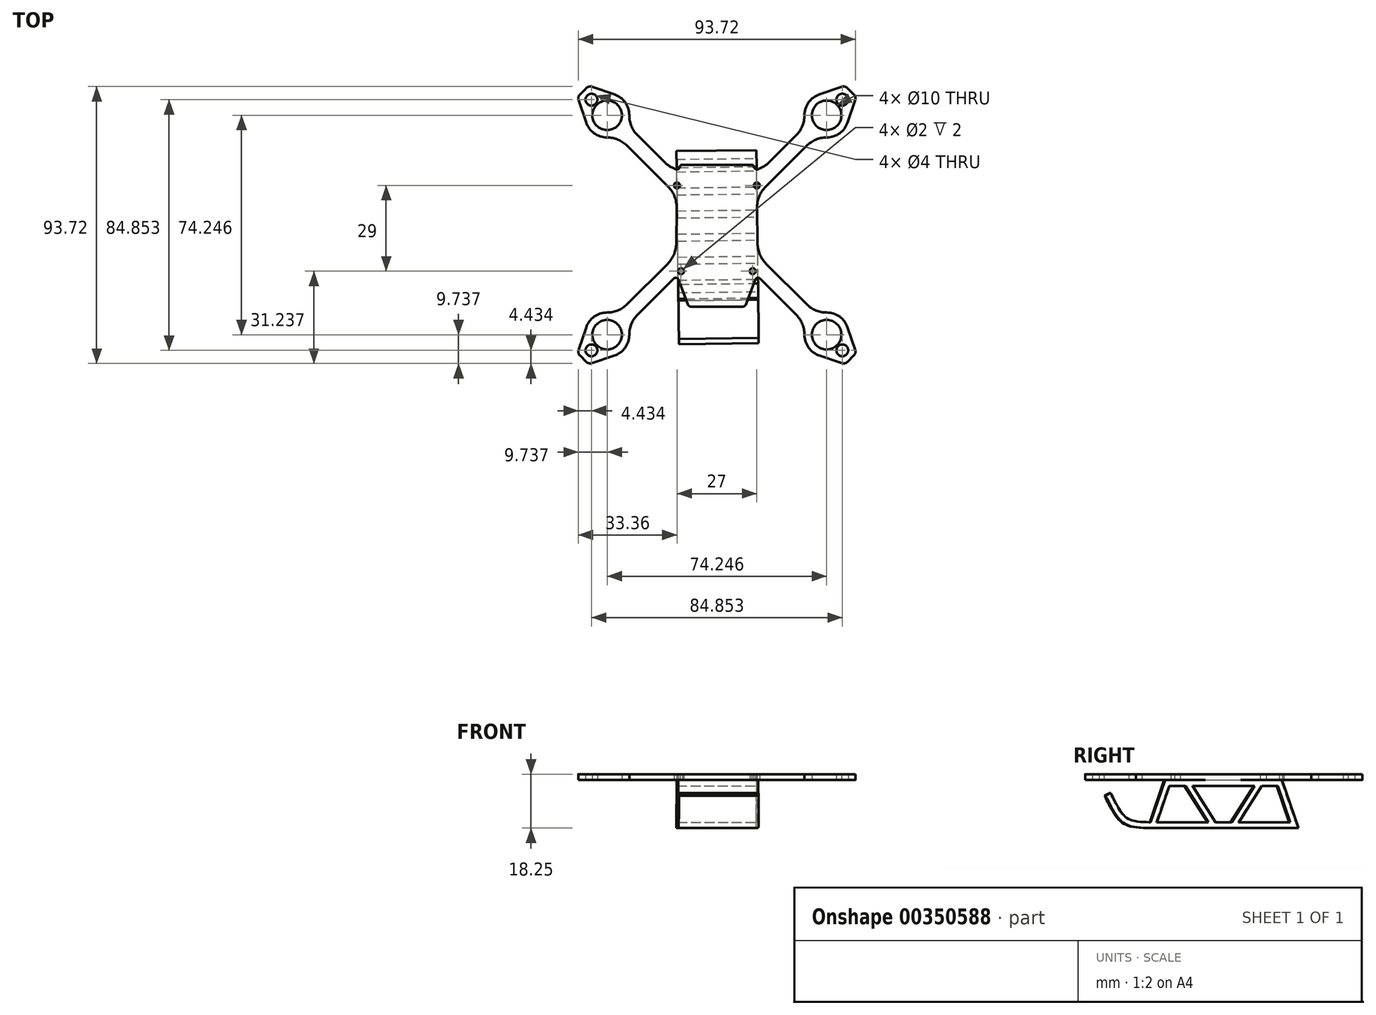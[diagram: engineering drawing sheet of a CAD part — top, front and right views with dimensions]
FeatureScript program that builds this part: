
annotation { "Feature Type Name" : "Feature", "Feature Type Description" : "" }
export const myFeature = defineFeature(function(context is Context, id is Id, definition is map)
    precondition{}
    {
        {
            var Q0;
            Q0=qCreatedBy(makeId("Top.planeOp"),FACE);
            var sketch = newSketch(context, id + "F0", { "sketchPlane" : qUnion([Q0])});
            skCircle(sketch, "E0", {"center": v(0, 0) * mm, "radius": 52.5 * mm, "construction": true});
            skLineSegment(sketch, "E1", {"start": v(0, 65.88) * mm, "end": v(0, -68.03) * mm, "construction": true});
            skLineSegment(sketch, "E2", {"start": v(68.65, 0) * mm, "end": v(-69.75, 0) * mm, "construction": true});
            skLineSegment(sketch, "E3.bottom", {"start": v(-52.5, 52.5) * mm, "end": v(52.5, 52.5) * mm, "construction": true});
            skLineSegment(sketch, "E3.top", {"start": v(-52.5, -52.5) * mm, "end": v(52.5, -52.5) * mm, "construction": true});
            skLineSegment(sketch, "E3.left", {"start": v(-52.5, 52.5) * mm, "end": v(-52.5, -52.5) * mm, "construction": true});
            skLineSegment(sketch, "E3.right", {"start": v(52.5, 52.5) * mm, "end": v(52.5, -52.5) * mm, "construction": true});
            skLineSegment(sketch, "E4", {"start": v(-52.5, 52.5) * mm, "end": v(52.5, -52.5) * mm, "construction": true});
            skLineSegment(sketch, "E5", {"start": v(52.5, 52.5) * mm, "end": v(-52.5, -52.5) * mm, "construction": true});
            skCircle(sketch, "E6.MirrorC", {"center": v(-37.12, 37.12) * mm, "radius": 5 * mm});
            skCircle(sketch, "E7.MirrorC", {"center": v(-37.12, -37.12) * mm, "radius": 5 * mm});
            skLineSegment(sketch, "E8", {"start": v(37.12, -37.12) * mm, "end": v(37.12, -15.62) * mm, "construction": true});
            skLineSegment(sketch, "E9", {"start": v(37.12, -15.62) * mm, "end": v(12.12, -15.62) * mm, "construction": true});
            skLineSegment(sketch, "E10", {"start": v(12.12, -15.62) * mm, "end": v(-12.12, -15.62) * mm, "construction": true});
            skLineSegment(sketch, "E11", {"start": v(-12.12, -15.62) * mm, "end": v(-37.12, -15.62) * mm, "construction": true});
            skLineSegment(sketch, "E12", {"start": v(-37.12, -37.12) * mm, "end": v(-37.12, 37.12) * mm, "construction": true});
            skLineSegment(sketch, "E13", {"start": v(37.12, 37.12) * mm, "end": v(37.12, -37.12) * mm, "construction": true});
            skLineSegment(sketch, "E14", {"start": v(37.12, -37.12) * mm, "end": v(-37.12, -37.12) * mm, "construction": true});
            skLineSegment(sketch, "E15", {"start": v(-37.12, 37.12) * mm, "end": v(37.12, 37.12) * mm, "construction": true});
            skCircle(sketch, "E16", {"center": v(-12.12, -15.62) * mm, "radius": 1 * mm});
            skCircle(sketch, "E17.MirrorC", {"center": v(12.12, -15.62) * mm, "radius": 1 * mm});
            skLineSegment(sketch, "E18", {"start": v(37.12, -15.62) * mm, "end": v(37.12, 13.38) * mm, "construction": true});
            skLineSegment(sketch, "E19", {"start": v(37.12, 13.38) * mm, "end": v(13.5, 13.38) * mm, "construction": true});
            skLineSegment(sketch, "E20", {"start": v(13.5, 13.38) * mm, "end": v(4.8, 13.38) * mm, "construction": true});
            skLineSegment(sketch, "E21", {"start": v(-13.5, 13.38) * mm, "end": v(-37.12, 13.38) * mm, "construction": true});
            skCircle(sketch, "E22", {"center": v(-13.5, 13.38) * mm, "radius": 1 * mm});
            skCircle(sketch, "E23.MirrorC", {"center": v(13.5, 13.38) * mm, "radius": 1 * mm});
            skArc(sketch, "E24", {"start": v(-37.12, -29.62) * mm, "mid": v(-41.5, -31.03) * mm, "end": v(-44.22, -34.71) * mm});
            skCircle(sketch, "E25", {"center": v(-42.43, -42.43) * mm, "radius": 2 * mm});
            skLineSegment(sketch, "E26.trimOffspring", {"start": v(-14.61, -18.15) * mm, "end": v(-26.83, -30.37) * mm});
            skLineSegment(sketch, "E27.trimOffspring", {"start": v(26.83, 30.37) * mm, "end": v(17.77, 21.3) * mm});
            skArc(sketch, "E28", {"start": v(-26.83, -30.37) * mm, "mid": v(-28.9, -33.47) * mm, "end": v(-29.62, -37.12) * mm});
            skLineSegment(sketch, "E29", {"start": v(-37.12, -37.12) * mm, "end": v(-17.54, -56.7) * mm, "construction": true});
            skLineSegment(sketch, "E30", {"start": v(-42.17, -46.76) * mm, "end": v(-34.71, -44.22) * mm});
            skLineSegment(sketch, "E31.MirrorCS", {"start": v(-46.76, -42.17) * mm, "end": v(-44.22, -34.71) * mm});
            skLineSegment(sketch, "E32", {"start": v(-46.28, -44.23) * mm, "end": v(-44.23, -46.28) * mm});
            skPoint(sketch, "E33.visualSharp", {"position": v(-43.35, -47.16) * mm});
            skArc(sketch, "E33.filletArc", {"start": v(-44.23, -46.28) * mm, "mid": v(-43.27, -46.81) * mm, "end": v(-42.17, -46.76) * mm});
            skPoint(sketch, "E34.visualSharp", {"position": v(-47.16, -43.35) * mm});
            skArc(sketch, "E34.filletArc", {"start": v(-46.76, -42.17) * mm, "mid": v(-46.81, -43.27) * mm, "end": v(-46.28, -44.23) * mm});
            skLineSegment(sketch, "E35", {"start": v(-43.84, -43.84) * mm, "end": v(-40.1, -47.58) * mm});
            skArc(sketch, "E36.MirrorCS", {"start": v(-30.37, -26.83) * mm, "mid": v(-33.47, -28.9) * mm, "end": v(-37.12, -29.62) * mm});
            skArc(sketch, "E37.trimOffspring", {"start": v(-34.71, -44.22) * mm, "mid": v(-31.03, -41.5) * mm, "end": v(-29.62, -37.12) * mm});
            skLineSegment(sketch, "E38.MirrorCS", {"start": v(26.83, -30.37) * mm, "end": v(11.4, -14.93) * mm});
            skLineSegment(sketch, "E39.MirrorCS", {"start": v(30.37, -26.83) * mm, "end": v(16.67, -13.14) * mm});
            skArc(sketch, "E40.MirrorCS", {"start": v(-30.37, 26.83) * mm, "mid": v(-33.47, 28.9) * mm, "end": v(-37.12, 29.62) * mm});
            skArc(sketch, "E41.MirrorCS", {"start": v(-26.83, 30.37) * mm, "mid": v(-28.9, 33.47) * mm, "end": v(-29.62, 37.12) * mm});
            skArc(sketch, "E42.MirrorCS", {"start": v(-34.71, 44.22) * mm, "mid": v(-31.03, 41.5) * mm, "end": v(-29.62, 37.12) * mm});
            skLineSegment(sketch, "E43.MirrorCS", {"start": v(-42.17, 46.76) * mm, "end": v(-34.71, 44.22) * mm});
            skLineSegment(sketch, "E44.MirrorCS", {"start": v(-46.28, 44.23) * mm, "end": v(-44.23, 46.28) * mm});
            skLineSegment(sketch, "E45.MirrorCS", {"start": v(-46.76, 42.17) * mm, "end": v(-44.22, 34.71) * mm});
            skArc(sketch, "E46.MirrorCS", {"start": v(-37.12, 29.62) * mm, "mid": v(-41.5, 31.03) * mm, "end": v(-44.22, 34.71) * mm});
            skArc(sketch, "E47.MirrorCS", {"start": v(-44.23, 46.28) * mm, "mid": v(-43.27, 46.81) * mm, "end": v(-42.17, 46.76) * mm});
            skArc(sketch, "E48.MirrorCS", {"start": v(-46.76, 42.17) * mm, "mid": v(-46.81, 43.27) * mm, "end": v(-46.28, 44.23) * mm});
            skCircle(sketch, "E49.MirrorC", {"center": v(-42.43, 42.43) * mm, "radius": 2 * mm});
            skLineSegment(sketch, "E50.MirrorCS", {"start": v(0, -65.88) * mm, "end": v(0, 68.03) * mm, "construction": true});
            skArc(sketch, "E51.MirrorCS", {"start": v(44.23, 46.28) * mm, "mid": v(43.27, 46.81) * mm, "end": v(42.17, 46.76) * mm});
            skLineSegment(sketch, "E52.MirrorCS", {"start": v(46.28, 44.23) * mm, "end": v(44.23, 46.28) * mm});
            skArc(sketch, "E53.MirrorCS", {"start": v(46.76, 42.17) * mm, "mid": v(46.81, 43.27) * mm, "end": v(46.28, 44.23) * mm});
            skLineSegment(sketch, "E54.MirrorCS", {"start": v(42.17, 46.76) * mm, "end": v(34.71, 44.22) * mm});
            skArc(sketch, "E55.MirrorCS", {"start": v(30.37, 26.83) * mm, "mid": v(33.47, 28.9) * mm, "end": v(37.12, 29.62) * mm});
            skLineSegment(sketch, "E56.MirrorCS", {"start": v(46.76, 42.17) * mm, "end": v(44.22, 34.71) * mm});
            skCircle(sketch, "E57.MirrorC", {"center": v(37.12, 37.12) * mm, "radius": 5 * mm});
            skArc(sketch, "E58.MirrorCS", {"start": v(34.71, 44.22) * mm, "mid": v(31.03, 41.5) * mm, "end": v(29.62, 37.12) * mm});
            skArc(sketch, "E59.MirrorCS", {"start": v(37.12, 29.62) * mm, "mid": v(41.5, 31.03) * mm, "end": v(44.22, 34.71) * mm});
            skArc(sketch, "E60.MirrorCS", {"start": v(26.83, 30.37) * mm, "mid": v(28.9, 33.47) * mm, "end": v(29.62, 37.12) * mm});
            skCircle(sketch, "E61.MirrorC", {"center": v(42.43, 42.43) * mm, "radius": 2 * mm});
            skArc(sketch, "E62.MirrorCS", {"start": v(46.76, -42.17) * mm, "mid": v(46.81, -43.27) * mm, "end": v(46.28, -44.23) * mm});
            skLineSegment(sketch, "E63.MirrorCS", {"start": v(46.28, -44.23) * mm, "end": v(44.23, -46.28) * mm});
            skArc(sketch, "E64.MirrorCS", {"start": v(44.23, -46.28) * mm, "mid": v(43.27, -46.81) * mm, "end": v(42.17, -46.76) * mm});
            skLineSegment(sketch, "E65.MirrorCS", {"start": v(43.84, -43.84) * mm, "end": v(40.1, -47.58) * mm});
            skLineSegment(sketch, "E66.MirrorCS", {"start": v(46.76, -42.17) * mm, "end": v(44.22, -34.71) * mm});
            skArc(sketch, "E67.MirrorCS", {"start": v(37.12, -29.62) * mm, "mid": v(41.5, -31.03) * mm, "end": v(44.22, -34.71) * mm});
            skCircle(sketch, "E68.MirrorC", {"center": v(42.43, -42.43) * mm, "radius": 2 * mm});
            skArc(sketch, "E69.MirrorCS", {"start": v(30.37, -26.83) * mm, "mid": v(33.47, -28.9) * mm, "end": v(37.12, -29.62) * mm});
            skArc(sketch, "E70.MirrorCS", {"start": v(34.71, -44.22) * mm, "mid": v(31.03, -41.5) * mm, "end": v(29.62, -37.12) * mm});
            skLineSegment(sketch, "E71.MirrorCS", {"start": v(42.17, -46.76) * mm, "end": v(34.71, -44.22) * mm});
            skCircle(sketch, "E72.MirrorC", {"center": v(37.12, -37.12) * mm, "radius": 5 * mm});
            skPoint(sketch, "E73.MirrorP", {"position": v(47.16, -43.35) * mm});
            skPoint(sketch, "E74.MirrorP", {"position": v(43.35, -47.16) * mm});
            skArc(sketch, "E75.MirrorCS", {"start": v(26.83, -30.37) * mm, "mid": v(28.9, -33.47) * mm, "end": v(29.62, -37.12) * mm});
            skPoint(sketch, "E76.orphan", {"position": v(35.83, -32.3) * mm});
            skPoint(sketch, "E77.orphan", {"position": v(32.3, -35.83) * mm});
            skPoint(sketch, "E78.orphan", {"position": v(35.83, 32.3) * mm});
            skPoint(sketch, "E79.orphan", {"position": v(32.3, 35.83) * mm});
            skLineSegment(sketch, "E80", {"start": v(-12.12, -15.62) * mm, "end": v(-12.12, -19.62) * mm, "construction": true});
            skLineSegment(sketch, "E81", {"start": v(-12.12, -19.62) * mm, "end": v(-12.12, -27.62) * mm, "construction": true});
            skLineSegment(sketch, "E82", {"start": v(-8.81, -27.62) * mm, "end": v(0, -27.62) * mm});
            skLineSegment(sketch, "E83", {"start": v(0, -27.62) * mm, "end": v(9.5, -27.62) * mm});
            skCircle(sketch, "E84", {"center": v(-12.12, -15.62) * mm, "radius": 2 * mm, "construction": true});
            skLineSegment(sketch, "E85", {"start": v(-12.97, -18.5) * mm, "end": v(-9.75, -26.98) * mm});
            skArc(sketch, "E86.filletArc", {"start": v(-12.97, -18.5) * mm, "mid": v(-13.7, -17.88) * mm, "end": v(-14.61, -18.15) * mm});
            skPoint(sketch, "E87.visualSharp", {"position": v(-9.5, -27.62) * mm});
            skArc(sketch, "E87.filletArc", {"start": v(-9.75, -26.98) * mm, "mid": v(-9.38, -27.45) * mm, "end": v(-8.81, -27.62) * mm});
            skArc(sketch, "E88.MirrorCS", {"start": v(9.75, -26.98) * mm, "mid": v(9.38, -27.45) * mm, "end": v(8.81, -27.62) * mm});
            skArc(sketch, "E89.MirrorCS", {"start": v(12.97, -18.5) * mm, "mid": v(13.7, -17.88) * mm, "end": v(14.61, -18.15) * mm});
            skLineSegment(sketch, "E90.MirrorCS", {"start": v(12.97, -18.5) * mm, "end": v(9.75, -26.98) * mm});
            skLineSegment(sketch, "E91.trimOffspring", {"start": v(-16.52, 12.99) * mm, "end": v(-30.37, 26.83) * mm});
            skLineSegment(sketch, "E92.trimOffspring", {"start": v(-16.67, -13.14) * mm, "end": v(-30.37, -26.83) * mm});
            skLineSegment(sketch, "E93.MirrorCS", {"start": v(16.52, 12.99) * mm, "end": v(30.37, 26.83) * mm});
            skLineSegment(sketch, "E94.trimOffspring", {"start": v(-17.77, 21.3) * mm, "end": v(-26.83, 30.37) * mm});
            skLineSegment(sketch, "E95", {"start": v(13.75, -6.2) * mm, "end": v(13.6, 5.8) * mm});
            skArc(sketch, "E96.filletArc", {"start": v(13.75, -6.2) * mm, "mid": v(14.53, -9.95) * mm, "end": v(16.67, -13.14) * mm});
            skPoint(sketch, "E97.newPointB", {"position": v(3.54, 0) * mm});
            skArc(sketch, "E97.filletArc", {"start": v(16.52, 12.99) * mm, "mid": v(14.33, 9.69) * mm, "end": v(13.6, 5.8) * mm});
            skArc(sketch, "E98.MirrorCS", {"start": v(-13.75, -6.2) * mm, "mid": v(-14.53, -9.95) * mm, "end": v(-16.67, -13.14) * mm});
            skLineSegment(sketch, "E99.MirrorCS", {"start": v(-13.75, -6.2) * mm, "end": v(-13.6, 5.8) * mm});
            skArc(sketch, "E100.MirrorCS", {"start": v(-16.52, 12.99) * mm, "mid": v(-14.33, 9.69) * mm, "end": v(-13.6, 5.8) * mm});
            skPoint(sketch, "E101.orphan", {"position": v(-3.54, 0) * mm});
            skLineSegment(sketch, "E102", {"start": v(-5.03, 13.38) * mm, "end": v(-5.03, 20.38) * mm, "construction": true});
            skLineSegment(sketch, "E103", {"start": v(4.8, 13.38) * mm, "end": v(4.8, 18.38) * mm, "construction": true});
            skArc(sketch, "E104.filletArc", {"start": v(-17.77, 21.3) * mm, "mid": v(-15.93, 19.86) * mm, "end": v(-13.81, 18.87) * mm});
            skLineSegment(sketch, "E105.bottom", {"start": v(12.5, 13.38) * mm, "end": v(4.8, 13.38) * mm});
            skLineSegment(sketch, "E105.top", {"start": v(11.84, 20.38) * mm, "end": v(0, 20.38) * mm});
            skLineSegment(sketch, "E105.right", {"start": v(0, 13.38) * mm, "end": v(0, 20.38) * mm});
            skLineSegment(sketch, "E106.MirrorCS", {"start": v(-11.66, 20.38) * mm, "end": v(0, 20.38) * mm});
            skPoint(sketch, "E107.newPointA", {"position": v(-12.5, 13.38) * mm});
            skArc(sketch, "E107.filletArc", {"start": v(-13.81, 18.87) * mm, "mid": v(-12.91, 19.01) * mm, "end": v(-12.5, 19.82) * mm});
            skPoint(sketch, "E108.visualSharp", {"position": v(-12.5, 20.38) * mm});
            skArc(sketch, "E109.MirrorCS", {"start": v(13.81, 18.87) * mm, "mid": v(12.91, 19.01) * mm, "end": v(12.5, 19.82) * mm});
            skArc(sketch, "E110", {"start": v(-11.66, 20.38) * mm, "mid": v(-12.18, 20.25) * mm, "end": v(-12.5, 19.82) * mm});
            skArc(sketch, "E111.MirrorCS", {"start": v(11.66, 20.38) * mm, "mid": v(12.18, 20.25) * mm, "end": v(12.5, 19.82) * mm});
            skArc(sketch, "E112.trimOffspring", {"start": v(13.81, 18.87) * mm, "mid": v(15.93, 19.86) * mm, "end": v(17.77, 21.3) * mm});
            skPoint(sketch, "E113.orphan", {"position": v(12.5, 20.38) * mm});
            skLineSegment(sketch, "E114.trimOffspring", {"start": v(0, 13.38) * mm, "end": v(-13.5, 13.38) * mm, "construction": true});
            skSolve(sketch);
        }
        {
            var Q0;
            Q0=makeQuery(id+"F0.imprint","IMPRINT",FACE,{"disambiguationData":[TD([[makeQuery(id+"F0.imprint","IMPRINT",EDGE,{"derivedFrom":sQuery(id+"F0.wireOp",EDGE,"E6.MirrorC")}),-1.0]])]});
            extrude(context, id + "F1", {"entities" : qUnion([Q0]), "depth" : 2 * mm});
        }
        {
            var Q0;
            Q0=makeQuery(id+"F1.opExtrude","SWEPT_FACE",FACE,{"disambiguationData":[OSD([sQuery(id+"F0.wireOp",EDGE,"E95")])]});
            var sketch = newSketch(context, id + "F2", { "sketchPlane" : qUnion([Q0])});
            skPoint(sketch, "E115.endSnap0", {"position": v(-0.37, 2) * mm});
            skLineSegment(sketch, "E116", {"start": v(-25.46, -16.25) * mm, "end": v(25.2, -16.25) * mm});
            skLineSegment(sketch, "E117", {"start": v(25.2, -16.25) * mm, "end": v(19.58, 0) * mm});
            skLineSegment(sketch, "E118.MirrorCS", {"start": v(-25.53, -16.25) * mm, "end": v(-25.53, -16.24) * mm});
            skFitSpline(sketch, "E119", {"points": [v(-25.46, -16.25) * mm, v(-35.92, -12.66) * mm, v(-40.14, -5.29) * mm], "startDerivative": vector(-35.1, 1.06) * mm, "endDerivative": vector(-4.05, 7.69) * mm});
            skLineSegment(sketch, "E120", {"start": v(-19.93, 0) * mm, "end": v(19.58, 0) * mm});
            skLineSegment(sketch, "E121.0", {"start": v(-18.5, -2) * mm, "end": v(18.16, -2) * mm});
            skLineSegment(sketch, "E122.0", {"start": v(-22.73, -14.25) * mm, "end": v(-18.5, -2) * mm});
            skLineSegment(sketch, "E123.trimOffspring", {"start": v(22.38, -14.25) * mm, "end": v(18.16, -2) * mm});
            skLineSegment(sketch, "E124.trimOffspring", {"start": v(-22.73, -14.25) * mm, "end": v(22.38, -14.25) * mm});
            skFitSpline(sketch, "E125.0", {"points": [v(-25.4, -14.25) * mm, v(-26.83, -14.2) * mm, v(-28.6, -14.1) * mm, v(-30.36, -13.83) * mm, v(-31.4, -13.57) * mm, v(-32.2, -13.27) * mm, v(-32.85, -12.9) * mm, v(-33.43, -12.45) * mm, v(-33.91, -11.96) * mm, v(-34.32, -11.46) * mm, v(-34.74, -10.9) * mm, v(-35.3, -10.07) * mm, v(-35.94, -9) * mm, v(-36.56, -7.88) * mm, v(-37.13, -6.8) * mm, v(-37.63, -5.81) * mm, v(-38.05, -4.97) * mm, v(-38.27, -4.54) * mm, v(-38.37, -4.35) * mm]});
            skLineSegment(sketch, "E126", {"start": v(-25.4, -14.25) * mm, "end": v(-24.84, -14.25) * mm});
            skLineSegment(sketch, "E127", {"start": v(-38.37, -4.35) * mm, "end": v(-40.14, -5.29) * mm});
            skLineSegment(sketch, "E128.trimOffspring", {"start": v(-24.84, -14.25) * mm, "end": v(-19.93, 0) * mm});
            skLineSegment(sketch, "E129", {"start": v(-13.07, -2) * mm, "end": v(-5.27, -14.25) * mm});
            skLineSegment(sketch, "E130.0", {"start": v(-10.7, -2) * mm, "end": v(-3.41, -13.44) * mm});
            skLineSegment(sketch, "E131", {"start": v(-3.41, -13.44) * mm, "end": v(-2.9, -14.25) * mm});
            skLineSegment(sketch, "E132.MirrorCS", {"start": v(10.36, -2) * mm, "end": v(3.07, -13.44) * mm});
            skLineSegment(sketch, "E133.MirrorCS", {"start": v(12.73, -2) * mm, "end": v(4.93, -14.25) * mm});
            skLineSegment(sketch, "E134.MirrorCS", {"start": v(3.07, -13.44) * mm, "end": v(2.56, -14.25) * mm});
            skSolve(sketch);
        }
        {
            var Q0;
            {var subQ15=sQuery(id+"F2.wireOp",EDGE,"E116");Q0=makeQuery(id+"F2.imprint","IMPRINT",FACE,{"disambiguationData":[TD([[makeQuery(id+"F2.imprint","IMPRINT",EDGE,{"derivedFrom":subQ15}),1.0]])]});}
            var Q1;
            {var subQ1=sQuery(id+"F2.wireOp",EDGE,"E129");Q1=makeQuery(id+"F2.imprint","IMPRINT",FACE,{"disambiguationData":[TD([[makeQuery(id+"F2.imprint","IMPRINT",EDGE,{"derivedFrom":subQ1}),1.0]])]});}
            var Q2;
            {var subQ0=sQuery(id+"F2.wireOp",EDGE,"E132.MirrorCS");Q2=makeQuery(id+"F2.imprint","IMPRINT",FACE,{"disambiguationData":[TD([[makeQuery(id+"F2.imprint","IMPRINT",EDGE,{"derivedFrom":subQ0}),1.0]])]});}
            extrude(context, id + "F3", {"entities" : qUnion([Q0, Q1, Q2]), "operationType" : NewBodyOperationType.ADD, "oppositeDirection" : true, "depth" : 27 * mm});
        }
    });
